# Revit family: Hammerkopfschraube 35
name_source: partatom
category: HLS-Bauteile
revit_build: Autodesk Revit 2017 (Build: 20190507_1515(x64)
units: mm (PartAtom-declared; Revit-internal decimal feet)

## family parameters
Arbeitsebenenbasiert = Nein
Beim Laden mit Abzugskörper schneiden = Nein
Bemaßung runder Anschluss = Durchmesser verwenden
Gemeinsam genutzt = Ja
Immer vertikal = Nein
Raumberechnungspunkt = Nein
Teiletyp = Normal

## types (17) — shared parameters
Anzugsmoment XL100 = 0.00 kN-m
Anzugsmoment XL80 = 0.00 kN-m
Fabrikat = MEFA
Firma = MEFA Befestigungs- und Montagesysteme GmbH
Material = Stahl
Materialname = S235
Mengeneinheit = St
Oberflaeche = galvanisch verzinkt
Profil = C-Profil

## per-type parameters (varying)
| type | Artikelnummer | Baulänge | Breite Hammerkopf | Durchmesser U-Scheibe | EAN | Gewicht | Gewicht pro Bauteil | Gewinde | Gewindeplatten | Gewindestift | H | H1 | Kurztext1 | Kurztext2 | Länge Gewinde | Länge Hammerkopf | Muttern | NL | Nutzlänge | Profiltyp | Stärke Hammerkopf | Stärke Scheibe | Unterlegscheibe | vpe |
| Hammerkopfschraube M 8x 25 | 0692320 | 18 mm | 17 mm | 25 mm | 4250928415691 | 0.03 kg | 0.03 kg | M8 | MEFA Gewindeplatte Vierkant : MEFA Gewindeplatte Vierkant 17x 17x 5 M 8 | Gewindestifte : Gewindestift M8x25 | 25 mm  [stored 0.082021 ft] | 5 mm  [stored 0.0164042 ft] | Hammerkopf C-Profil 22 | M8 x 25 mm | 25 mm  [stored 0.082021 ft] | 17 mm | Sechskantmutter : Sechskantmutter M8 | 10 mm  [stored 0.0328084 ft] | 9,5 mm | 22 | 5 mm | 2 mm | Unterlegscheibe : Unterlegscheibe, verstärkt 8.4x24x2.0 | 100 St |
| Hammerkopfschraube M 8x 30 für Profil 22 | 0692328 | 23 mm | 17 mm | 25 mm | 4250928415707 | 0.03 kg | 0.03 kg | M8 | MEFA Gewindeplatte Vierkant : MEFA Gewindeplatte Vierkant 17x 17x 5 M 8 | Gewindestifte : Gewindestift M8x30 | 30 mm  [stored 0.0984252 ft] | 5 mm  [stored 0.0164042 ft] | Hammerkopf C-Profil 22 | M8 x 30 mm | 30 mm  [stored 0.0984252 ft] | 17 mm | Sechskantmutter : Sechskantmutter M8 | 15 mm  [stored 0.0492126 ft] | 14,5 mm | 22 | 5 mm | 2 mm | Unterlegscheibe : Unterlegscheibe, verstärkt 8.4x24x2.0 | 100 St |
| Hammerkopfschraube M 8x 40 für Profil 22 | 0692330 | 23 mm | 17 mm | 25 mm | 4250928415707 | 0.03 kg | 0.03 kg | M8 | MEFA Gewindeplatte Vierkant : MEFA Gewindeplatte Vierkant 17x 17x 5 M 8 | Gewindestifte : Gewindestift M8x40 | 40 mm  [stored 0.131234 ft] | 5 mm  [stored 0.0164042 ft] | Hammerkopf C-Profil 22 | M8 x 30 mm | 30 mm  [stored 0.0984252 ft] | 17 mm | Sechskantmutter : Sechskantmutter M8 | 25 mm  [stored 0.082021 ft] | 14,5 mm | 22 | 5 mm | 2 mm | Unterlegscheibe : Unterlegscheibe, verstärkt 8.4x24x2.0 | 100 St |
| Hammerkopfschraube M10x 40 für Profil 22 | 0693340 | 33 mm | 17 mm | 20 mm | 4250928415721 | 0.04 kg | 0.04 kg | M10 | MEFA Gewindeplatte Vierkant : MEFA Gewindeplatte Vierkant 17x 17x 5 M10 | Gewindestifte : Gewindestift M10x40 | 40 mm  [stored 0.131234 ft] | 5 mm  [stored 0.0164042 ft] | Hammerkopf C-Profil 22 | M10 x 40 mm | 40 mm  [stored 0.131234 ft] | 17 mm | Sechskantmutter : Sechskantmutter M10 | 23 mm  [stored 0.0754593 ft] | 23 mm | 22 | 5 mm | 2 mm | Unterlegscheibe : Unterlegscheibe 10.5x20x2 | 100 St |
| Hammerkopfschraube M 8x 20 | 0695289 | 15 mm | 13 mm | 25 mm | 4250928415738 | 0.02 kg | 0.02 kg | M8 | MEFA Gewindeplatte 28x15 : MEFA Gewindeplatte 28x15 M 8 | Gewindestifte : Gewindestift M8x20 | 20 mm  [stored 0.0656168 ft] | 4 mm  [stored 0.0131234 ft] | Hammerkopf C-Profil 27 | M8 x 20 mm | 20 mm  [stored 0.0656168 ft] | 24 mm | Sechskantmutter : Sechskantmutter M8 | 6 mm  [stored 0.019685 ft] | 6,3 mm | 27 | 4 mm | 2 mm | Unterlegscheibe : Unterlegscheibe, verstärkt 8.4x24x2.0 | 100 St |
| Hammerkopfschraube M 8x 30 für Profil 27 | 0695300 | 25 mm | 13 mm | 25 mm | 4250928415745 | 0.03 kg | 0.03 kg | M8 | MEFA Gewindeplatte 28x15 : MEFA Gewindeplatte 28x15 M 8 | Gewindestifte : Gewindestift M8x30 | 30 mm  [stored 0.0984252 ft] | 4 mm  [stored 0.0131234 ft] | Hammerkopf C-Profil 27 | M8 x 30 mm | 30 mm  [stored 0.0984252 ft] | 24 mm | Sechskantmutter : Sechskantmutter M8 | 16 mm  [stored 0.0524934 ft] | 16,3 mm | 27 | 4 mm | 2 mm | Unterlegscheibe : Unterlegscheibe, verstärkt 8.4x24x2.0 | 100 St |
| Hammerkopfschraube M 8x 40 für Profil 27 | 0695327 | 35 mm | 13 mm | 25 mm | 4250928415752 | 0.03 kg | 0.03 kg | M8 | MEFA Gewindeplatte 28x15 : MEFA Gewindeplatte 28x15 M 8 | Gewindestifte : Gewindestift M8x40 | 40 mm  [stored 0.131234 ft] | 4 mm  [stored 0.0131234 ft] | Hammerkopf C-Profil 27 | M8 x 40 mm | 40 mm  [stored 0.131234 ft] | 24 mm | Sechskantmutter : Sechskantmutter M8 | 26 mm | 26,3 mm | 27 | 4 mm | 2 mm | Unterlegscheibe : Unterlegscheibe, verstärkt 8.4x24x2.0 | 100 St |
| Hammerkopfschraube M 8x 30 für Profil 35 | 0697044 | 22 mm | 18 mm | 35 mm | 4250928415769 | 0.06 kg | 0.06 kg | M8 | MEFA Gewindeplatte 38x17 : MEFA Gewindeplatte 38x17 M 8 | Gewindestifte : Gewindestift M8x30 | 30 mm  [stored 0.0984252 ft] | 6 mm  [stored 0.019685 ft] | Hammerkopf C-Profil 35 | M8 x 30 mm | 30 mm  [stored 0.0984252 ft] | 35 mm | Sechskantmutter : Sechskantmutter M8 | 13 mm  [stored 0.0426509 ft] | 12,5 mm | 35, Stex 35 | 6 mm | 3 mm | Unterlegscheibe : Unterlegscheibe, verstärkt 8.4x35x3 | 50 St |
| Hammerkopfschraube M 8x 40 für Profil 35 | 0697051 | 32 mm | 18 mm | 35 mm | 4250928415776 | 0.06 kg | 0.06 kg | M8 | MEFA Gewindeplatte 38x17 : MEFA Gewindeplatte 38x17 M 8 | Gewindestifte : Gewindestift M8x40 | 40 mm  [stored 0.131234 ft] | 6 mm  [stored 0.019685 ft] | Hammerkopf C-Profil 35 | M8 x 40 mm | 40 mm  [stored 0.131234 ft] | 35 mm | Sechskantmutter : Sechskantmutter M8 | 23 mm  [stored 0.0754593 ft] | 22,5 mm | 35, Stex 35 | 6 mm | 3 mm | Unterlegscheibe : Unterlegscheibe, verstärkt 8.4x35x3 | 50 St |
| Hammerkopfschraube M 8x 50 | 0697060 | 42 mm | 18 mm | 35 mm | 4250928415783 | 0.07 kg | 0.07 kg | M8 | MEFA Gewindeplatte 38x17 : MEFA Gewindeplatte 38x17 M 8 | Gewindestifte : Gewindestift M8x50 | 50 mm  [stored 0.164042 ft] | 6 mm  [stored 0.019685 ft] | Hammerkopf C-Profil 35 | M8 x 50 mm | 50 mm  [stored 0.164042 ft] | 35 mm | Sechskantmutter : Sechskantmutter M8 | 33 mm | 32,5 mm | 35, Stex 35 | 6 mm | 3 mm | Unterlegscheibe : Unterlegscheibe, verstärkt 8.4x35x3 | 50 St |
| Hammerkopfschraube M10x 30 | 0697540 | 22 mm | 18 mm | 35 mm | 4250928415806 | 0.07 kg | 0.07 kg | M10 | MEFA Gewindeplatte 38x17 : MEFA Gewindeplatte 38x17 M10 | Gewindestifte : Gewindestift M10x30 | 30 mm  [stored 0.0984252 ft] | 6 mm  [stored 0.019685 ft] | Hammerkopf C-Profil 35 | M10 x 30 mm | 30 mm  [stored 0.0984252 ft] | 35 mm | Sechskantmutter : Sechskantmutter M10 | 11 mm | 10,5 mm | 35, Stex 35 | 6 mm | 3 mm | Unterlegscheibe : Unterlegscheibe, verstärkt 10.5x35x3 | 50 St |
| Hammerkopfschraube M10x 40 | 0697560 | 32 mm | 18 mm | 35 mm | 4250928415813 | 0.07 kg | 0.07 kg | M10 | MEFA Gewindeplatte 38x17 : MEFA Gewindeplatte 38x17 M10 | Gewindestifte : Gewindestift M10x40 | 40 mm  [stored 0.131234 ft] | 6 mm  [stored 0.019685 ft] | Hammerkopf C-Profil 35 | M10 x 40 mm | 40 mm  [stored 0.131234 ft] | 35 mm | Sechskantmutter : Sechskantmutter M10 | 21 mm  [stored 0.0688976 ft] | 21 mm | 35, Stex 35 | 6 mm | 3 mm | Unterlegscheibe : Unterlegscheibe, verstärkt 10.5x35x3 | 50 St |
| Hammerkopfschraube M10x 50 | 0697570 | 42 mm | 18 mm | 35 mm | 4250928415820 | 0.08 kg | 0.08 kg | M10 | MEFA Gewindeplatte 38x17 : MEFA Gewindeplatte 38x17 M10 | Gewindestifte : Gewindestift M10x50 | 50 mm  [stored 0.164042 ft] | 6 mm  [stored 0.019685 ft] | Hammerkopf C-Profil 35 | M10 x 50 mm | 50 mm  [stored 0.164042 ft] | 35 mm | Sechskantmutter : Sechskantmutter M10 | 31 mm  [stored 0.101706 ft] | 31 mm | 35, Stex 35 | 6 mm | 3 mm | Unterlegscheibe : Unterlegscheibe, verstärkt 10.5x35x3 | 50 St |
| Hammerkopfschraube M10x 70 | 0697590 | 62 mm | 18 mm | 35 mm | 4250928415837 | 0.09 kg | 0.09 kg | M10 | MEFA Gewindeplatte 38x17 : MEFA Gewindeplatte 38x17 M10 | Gewindestifte : Gewindestift M10x70 | 70 mm  [stored 0.229659 ft] | 6 mm  [stored 0.019685 ft] | Hammerkopf C-Profil 35 | M10 x 70 mm | 70 mm  [stored 0.229659 ft] | 35 mm | Sechskantmutter : Sechskantmutter M10 | 51 mm | 51 mm | 35, Stex 35 | 6 mm | 3 mm | Unterlegscheibe : Unterlegscheibe, verstärkt 10.5x35x3 | 50 St |
| Hammerkopfschraube M12x 35 | 0698040 | 27 mm | 18 mm | 37 mm | 4250928415844 | 0.09 kg | 0.09 kg | M12 | MEFA Gewindeplatte 38x17 : MEFA Gewindeplatte 38x17 M12 | Gewindestifte : Gewindestift M12x35 | 35 mm  [stored 0.114829 ft] | 6 mm  [stored 0.019685 ft] | Hammerkopf C-Profil 35 | M12 x 35 mm | 35 mm  [stored 0.114829 ft] | 35 mm | Sechskantmutter : Sechskantmutter M12 | 14 mm  [stored 0.0459318 ft] | 14 mm | 35, Stex 35 | 6 mm | 3 mm | Unterlegscheibe : Unterlegscheibe, verstärkt 13x37x3 | 50 St |
| Hammerkopfschraube M12x 50 | 0698050 | 42 mm | 18 mm | 37 mm | 4250928415851 | 0.10 kg | 0.10 kg | M12 | MEFA Gewindeplatte 38x17 : MEFA Gewindeplatte 38x17 M12 | Gewindestifte : Gewindestift M12x50 | 50 mm  [stored 0.164042 ft] | 6 mm  [stored 0.019685 ft] | Hammerkopf C-Profil 35 | M12 x 50 mm | 50 mm  [stored 0.164042 ft] | 35 mm | Sechskantmutter : Sechskantmutter M12 | 29 mm  [stored 0.0951444 ft] | 29 mm | 35, Stex 35 | 6 mm | 3 mm | Unterlegscheibe : Unterlegscheibe, verstärkt 13x37x3 | 50 St |
| Hammerkopfschraube M12x 70 | 0698070 | 62 mm | 18 mm | 37 mm | 4250928415868 | 0.11 kg | 0.11 kg | M12 | MEFA Gewindeplatte 38x17 : MEFA Gewindeplatte 38x17 M12 | Gewindestifte : Gewindestift M12x70 | 70 mm  [stored 0.229659 ft] | 6 mm  [stored 0.019685 ft] | Hammerkopf C-Profil 35 | M12 x 70 mm | 70 mm  [stored 0.229659 ft] | 35 mm | Sechskantmutter : Sechskantmutter M12 | 49 mm  [stored 0.160761 ft] | 49 mm | 35, Stex 35 | 6 mm | 3 mm | Unterlegscheibe : Unterlegscheibe, verstärkt 13x37x3 | 50 St |

note: [stored X ft] marks values corroborated as IEEE doubles in the binary element streams (Revit-internal decimal feet)

## geometry (parser evidence)
native form markers: Sweep x3
no freeform markers — native parametric forms only
